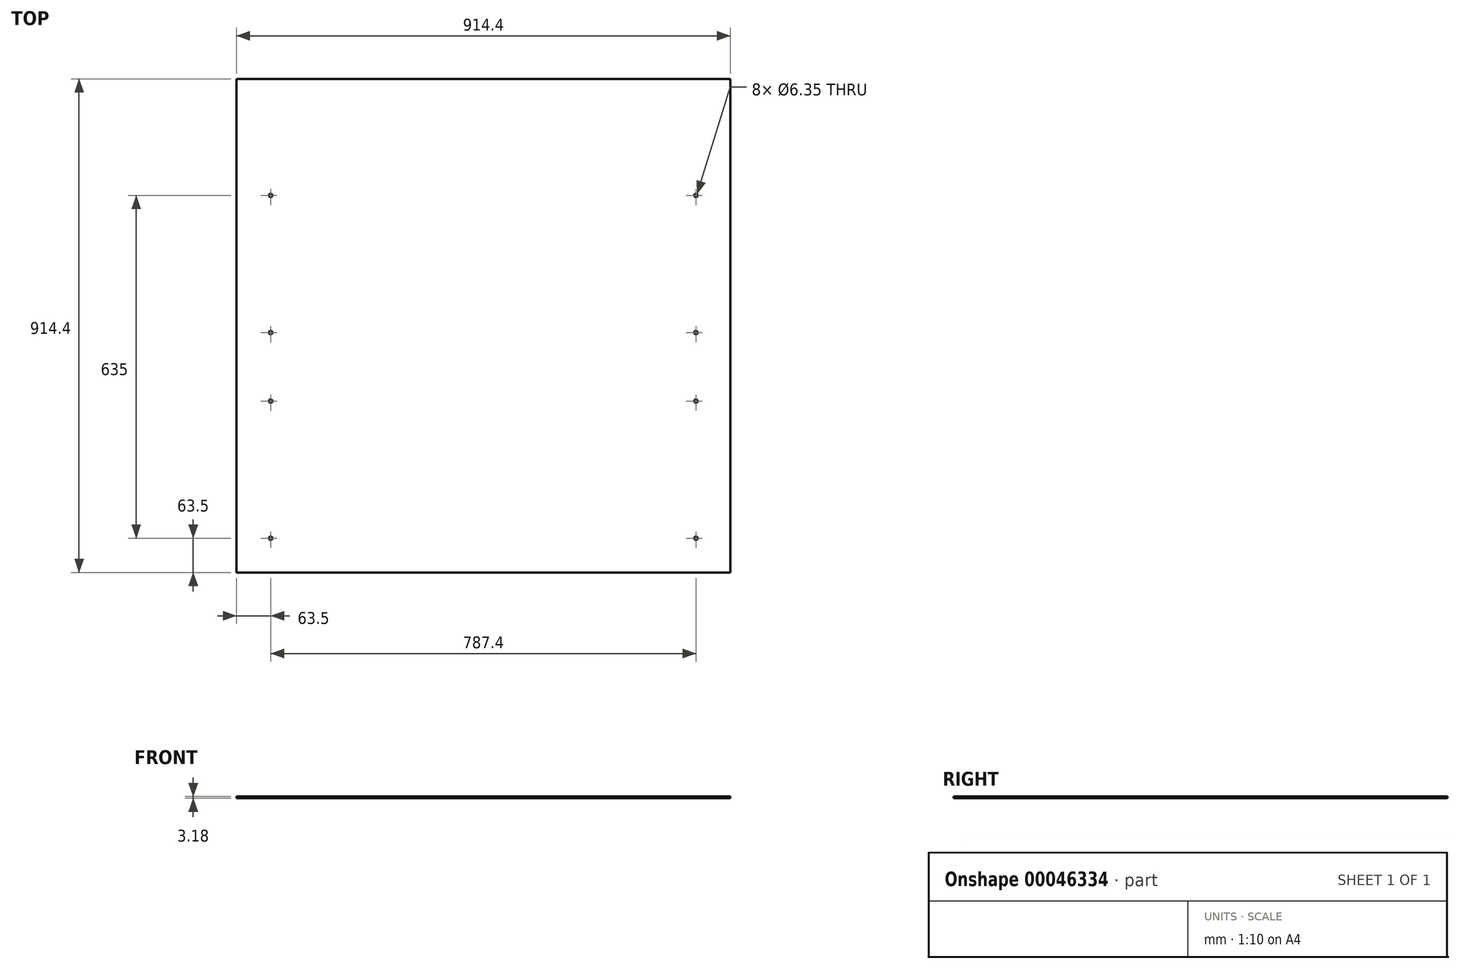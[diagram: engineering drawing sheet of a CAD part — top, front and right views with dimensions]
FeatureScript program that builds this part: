
annotation { "Feature Type Name" : "Feature", "Feature Type Description" : "" }
export const myFeature = defineFeature(function(context is Context, id is Id, definition is map)
    precondition{}
    {
        {
            var Q0;
            Q0=qCreatedBy(makeId("Top.planeOp"),FACE);
            var sketch = newSketch(context, id + "F0", { "sketchPlane" : qUnion([Q0])});
            skLineSegment(sketch, "E0.rect.bottom", {"start": v(457.2, -457.2) * mm, "end": v(-457.2, -457.2) * mm});
            skLineSegment(sketch, "E0.rect.top", {"start": v(457.2, 457.2) * mm, "end": v(-457.2, 457.2) * mm});
            skLineSegment(sketch, "E0.rect.left", {"start": v(457.2, -457.2) * mm, "end": v(457.2, 457.2) * mm});
            skLineSegment(sketch, "E0.rect.right", {"start": v(-457.2, -457.2) * mm, "end": v(-457.2, 457.2) * mm});
            skPoint(sketch, "E0.rect.middle", {"position": v(0, 0) * mm});
            skCircle(sketch, "E1", {"center": v(-393.7, -393.7) * mm, "radius": 3.18 * mm});
            skCircle(sketch, "E2", {"center": v(393.7, -393.7) * mm, "radius": 3.18 * mm});
            skCircle(sketch, "E3", {"center": v(393.7, -139.7) * mm, "radius": 3.18 * mm});
            skCircle(sketch, "E4", {"center": v(-393.7, -139.7) * mm, "radius": 3.18 * mm});
            skCircle(sketch, "E5", {"center": v(-393.7, -12.7) * mm, "radius": 3.18 * mm});
            skCircle(sketch, "E6", {"center": v(-393.7, 241.3) * mm, "radius": 3.18 * mm});
            skCircle(sketch, "E7", {"center": v(393.7, 241.3) * mm, "radius": 3.18 * mm});
            skCircle(sketch, "E8", {"center": v(393.7, -12.7) * mm, "radius": 3.18 * mm});
            skSolve(sketch);
        }
        {
            var Q0;
            Q0=makeQuery(id+"F0.imprint","IMPRINT",FACE,{"disambiguationData":[TD([[makeQuery(id+"F0.imprint","IMPRINT",EDGE,{"derivedFrom":sQuery(id+"F0.wireOp",EDGE,"E0.rect.bottom")}),-1.0]])]});
            extrude(context, id + "F1", {"entities" : qUnion([Q0]), "depth" : 3.17 * mm});
        }
    });
